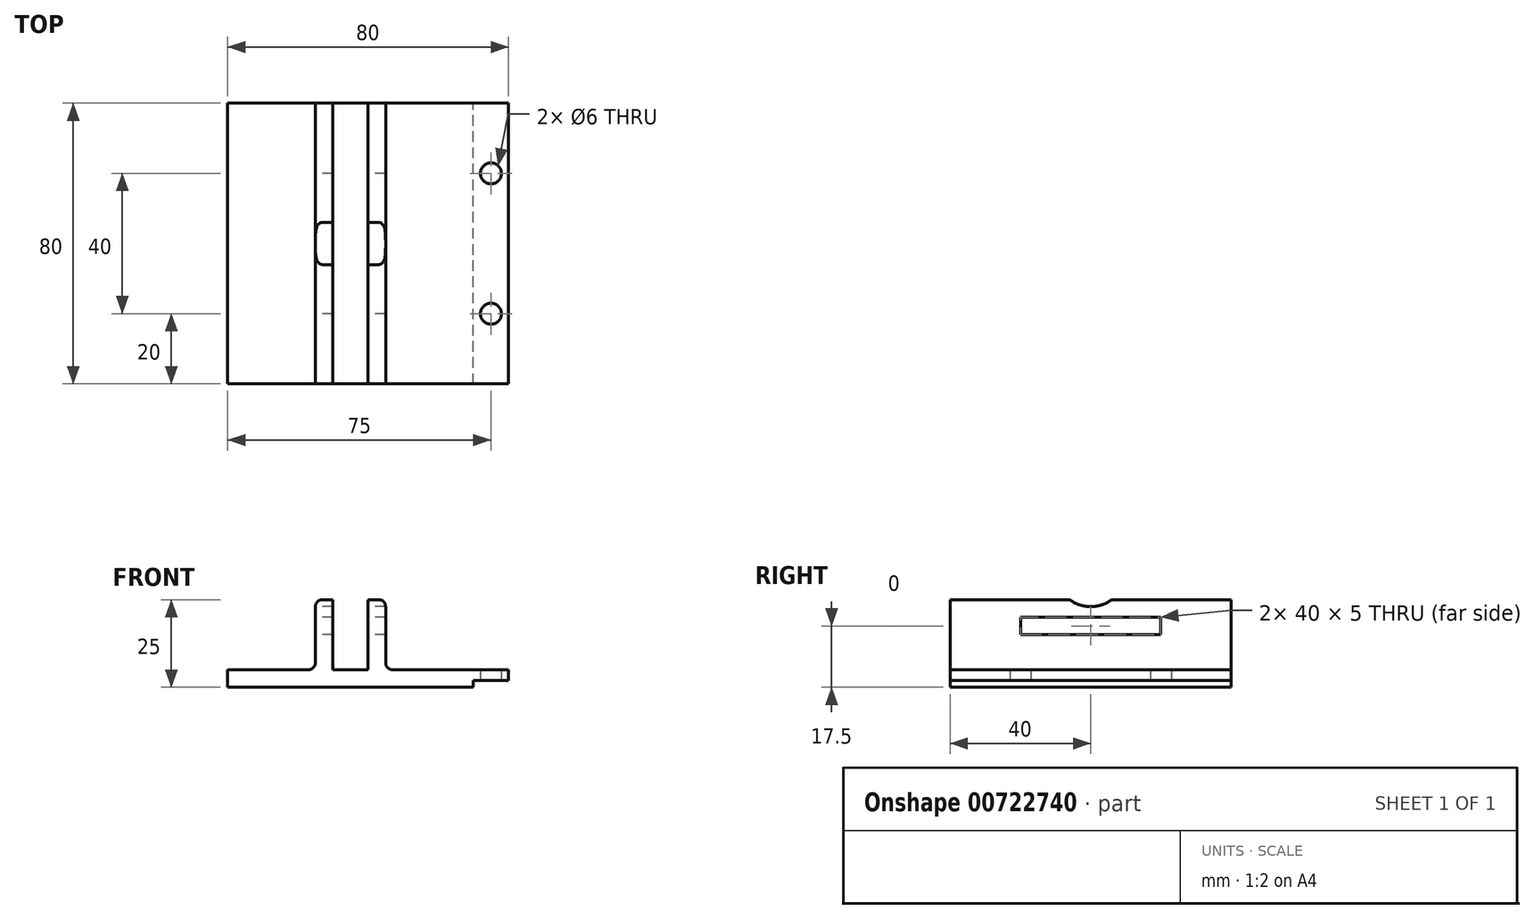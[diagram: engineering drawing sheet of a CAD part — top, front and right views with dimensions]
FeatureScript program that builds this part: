
annotation { "Feature Type Name" : "Feature", "Feature Type Description" : "" }
export const myFeature = defineFeature(function(context is Context, id is Id, definition is map)
    precondition{}
    {
        {
            var Q0;
            Q0=qCreatedBy(makeId("Front.planeOp"),FACE);
            var sketch = newSketch(context, id + "F0", { "sketchPlane" : qUnion([Q0])});
            skLineSegment(sketch, "E0.bottom", {"start": v(0, 0) * mm, "end": v(-10, 0) * mm, "construction": true});
            skLineSegment(sketch, "E0.top", {"start": v(0, 20) * mm, "end": v(-10, 20) * mm, "construction": true});
            skLineSegment(sketch, "E0.left", {"start": v(0, 0) * mm, "end": v(0, 20) * mm, "construction": true});
            skLineSegment(sketch, "E0.right", {"start": v(-10, 0) * mm, "end": v(-10, 20) * mm, "construction": true});
            skLineSegment(sketch, "E1.bottom", {"start": v(-10, 20) * mm, "end": v(-15, 20) * mm});
            skLineSegment(sketch, "E1.top", {"start": v(-10, 0) * mm, "end": v(-15, 0) * mm, "construction": true});
            skLineSegment(sketch, "E1.left", {"start": v(-10, 20) * mm, "end": v(-10, 0) * mm});
            skLineSegment(sketch, "E1.right", {"start": v(-15, 20) * mm, "end": v(-15, 0) * mm});
            skLineSegment(sketch, "E2.bottom", {"start": v(0, 20) * mm, "end": v(5, 20) * mm});
            skLineSegment(sketch, "E2.top", {"start": v(0, 0) * mm, "end": v(5, 0) * mm});
            skLineSegment(sketch, "E2.left", {"start": v(0, 20) * mm, "end": v(0, 0) * mm});
            skLineSegment(sketch, "E2.right", {"start": v(5, 20) * mm, "end": v(5, 0) * mm});
            skLineSegment(sketch, "E3.bottom", {"start": v(0, 0) * mm, "end": v(-40, 0) * mm});
            skLineSegment(sketch, "E3.top", {"start": v(0, -5) * mm, "end": v(-40, -5) * mm});
            skLineSegment(sketch, "E3.left", {"start": v(0, 0) * mm, "end": v(0, -5) * mm});
            skLineSegment(sketch, "E3.right", {"start": v(-40, 0) * mm, "end": v(-40, -5) * mm});
            skLineSegment(sketch, "E4.bottom", {"start": v(0, 0) * mm, "end": v(30, 0) * mm});
            skLineSegment(sketch, "E4.top", {"start": v(0, -5) * mm, "end": v(30, -5) * mm});
            skLineSegment(sketch, "E4.right", {"start": v(30, 0) * mm, "end": v(30, -5) * mm});
            skSolve(sketch);
        }
        {
            var Q0;
            Q0=qSketchRegion(id+"F0",true);
            extrude(context, id + "F1", {"entities" : qUnion([Q0]), "depth" : 80 * mm, "offsetDistance" : 25 * mm, "symmetric" : true});
        }
        {
            var Q0;
            Q0=makeQuery(id+"F1.opExtrude","SWEPT_EDGE",EDGE,{"disambiguationData":[OSD([sQuery(id+"F0.wireOp",EDGE,"E2.right"),sQuery(id+"F0.wireOp",EDGE,"E4.bottom")])]});
            var Q1;
            Q1=makeQuery(id+"F1.opExtrude","SWEPT_EDGE",EDGE,{"disambiguationData":[OSD([sQuery(id+"F0.wireOp",EDGE,"E1.right"),sQuery(id+"F0.wireOp",EDGE,"E3.bottom")])]});
            fillet(context, id + "F2", {"entities" : qUnion([Q0, Q1]), "radius" : 2 * mm, "tangentPropagation" : true, "allowEdgeOverflow" : false});
        }
        {
            var Q0;
            Q0=makeQuery(id+"F1.opExtrude","SWEPT_EDGE",EDGE,{"disambiguationData":[OSD([sQuery(id+"F0.wireOp",EDGE,"E1.bottom"),sQuery(id+"F0.wireOp",EDGE,"E1.right")])]});
            var Q1;
            Q1=makeQuery(id+"F1.opExtrude","SWEPT_EDGE",EDGE,{"disambiguationData":[OSD([sQuery(id+"F0.wireOp",EDGE,"E2.bottom"),sQuery(id+"F0.wireOp",EDGE,"E2.right")])]});
            fillet(context, id + "F3", {"entities" : qUnion([Q0, Q1]), "radius" : 2 * mm, "tangentPropagation" : true, "allowEdgeOverflow" : false});
        }
        {
            var Q0;
            Q0=makeQuery(id+"F1.opExtrude","SWEPT_FACE",FACE,{"disambiguationData":[OSD([sQuery(id+"F0.wireOp",EDGE,"E1.right")])]});
            var sketch = newSketch(context, id + "F4", { "sketchPlane" : qUnion([Q0])});
            skLineSegment(sketch, "E5", {"start": v(-40, 0) * mm, "end": v(-20, 0) * mm, "construction": true});
            skLineSegment(sketch, "E6", {"start": v(-20, 0) * mm, "end": v(-20, 10) * mm, "construction": true});
            skLineSegment(sketch, "E7.bottom", {"start": v(-20, 10) * mm, "end": v(20, 10) * mm});
            skLineSegment(sketch, "E7.top", {"start": v(-20, 15) * mm, "end": v(20, 15) * mm});
            skLineSegment(sketch, "E7.left", {"start": v(-20, 10) * mm, "end": v(-20, 15) * mm});
            skLineSegment(sketch, "E7.right", {"start": v(20, 10) * mm, "end": v(20, 15) * mm});
            skSolve(sketch);
        }
        {
            var Q0;
            Q0=qSketchRegion(id+"F4",true);
            extrude(context, id + "F5", {"entities" : qUnion([Q0]), "operationType" : NewBodyOperationType.REMOVE, "oppositeDirection" : true, "depth" : 25 * mm, "offsetDistance" : 25 * mm});
        }
        {
            var Q0;
            Q0=makeQuery(id+"F1.opExtrude","SWEPT_FACE",FACE,{"disambiguationData":[OSD([sQuery(id+"F0.wireOp",EDGE,"E4.bottom")])]});
            var sketch = newSketch(context, id + "F6", { "sketchPlane" : qUnion([Q0])});
            skLineSegment(sketch, "E8.bottom", {"start": v(30, 40) * mm, "end": v(40, 40) * mm});
            skLineSegment(sketch, "E8.top", {"start": v(30, -40) * mm, "end": v(40, -40) * mm});
            skLineSegment(sketch, "E8.left", {"start": v(30, 40) * mm, "end": v(30, -40) * mm});
            skLineSegment(sketch, "E8.right", {"start": v(40, 40) * mm, "end": v(40, -40) * mm});
            skSolve(sketch);
        }
        {
            var Q0;
            Q0 = qSketchRegion(id + "F6", true);
            extrude(context, id + "F7", {"entities" : qUnion([Q0]), "operationType" : NewBodyOperationType.ADD, "oppositeDirection" : true, "depth" : 3 * mm, "offsetDistance" : 25 * mm});
        }
        {
            var Q0;
            Q0=makeQuery(id+"F7.opExtrude","CAP_FACE",FACE,{"disambiguationData":[OSD([sQuery(id+"F6.wireOp",EDGE,"E8.bottom"),sQuery(id+"F6.wireOp",EDGE,"E8.top"),sQuery(id+"F6.wireOp",EDGE,"E8.left"),sQuery(id+"F6.wireOp",EDGE,"E8.right")])],"isStart":false});
            var sketch = newSketch(context, id + "F8", { "sketchPlane" : qUnion([Q0])});
            skLineSegment(sketch, "E9", {"start": v(30, 0) * mm, "end": v(35, 0) * mm, "construction": true});
            skLineSegment(sketch, "E10", {"start": v(35, 0) * mm, "end": v(35, 20) * mm, "construction": true});
            skCircle(sketch, "E11", {"center": v(35, 20) * mm, "radius": 3 * mm});
            skSolve(sketch);
        }
        {
            var Q0;
            Q0 = qSketchRegion(id + "F8", true);
            extrude(context, id + "F9", {"entities" : qUnion([Q0]), "oppositeDirection" : true, "depth" : 3 * mm, "offsetDistance" : 25 * mm});
        }
        {
            var Q0;
            Q0=makeQuery(id+"F9.opExtrude","SWEPT_BODY",BODY,{"disambiguationData":[OSD([sQuery(id+"F8.wireOp",EDGE,"E11")])]});
            var Q1;
            Q1=qCreatedBy(makeId("Front.planeOp"),FACE);
            mirror(context, id + "F10", {"entities" : qUnion([Q0]), "mirrorPlane" : qUnion([Q1])});
        }
        {
            var Q0;
            Q0=makeQuery(id+"F10.opPattern","COPY",BODY,{"derivedFrom":makeQuery(id+"F9.opExtrude","SWEPT_BODY",BODY,{"disambiguationData":[OSD([sQuery(id+"F8.wireOp",EDGE,"E11")])]}),"instanceName":"1"});
            var Q1;
            Q1=makeQuery(id+"F9.opExtrude","SWEPT_BODY",BODY,{"disambiguationData":[OSD([sQuery(id+"F8.wireOp",EDGE,"E11")])]});
            var Q2;
            Q2=makeQuery(id+"F1.opExtrude","SWEPT_BODY",BODY,{"disambiguationData":[OSD([sQuery(id+"F0.wireOp",EDGE,"E1.bottom"),sQuery(id+"F0.wireOp",EDGE,"E1.left"),sQuery(id+"F0.wireOp",EDGE,"E1.right"),sQuery(id+"F0.wireOp",EDGE,"E2.bottom"),sQuery(id+"F0.wireOp",EDGE,"E2.left"),sQuery(id+"F0.wireOp",EDGE,"E2.right"),sQuery(id+"F0.wireOp",EDGE,"E3.bottom"),sQuery(id+"F0.wireOp",EDGE,"E3.top"),sQuery(id+"F0.wireOp",EDGE,"E3.right"),sQuery(id+"F0.wireOp",EDGE,"E4.bottom"),sQuery(id+"F0.wireOp",EDGE,"E4.top"),sQuery(id+"F0.wireOp",EDGE,"E4.right")])]});
            booleanBodies(context, id + "F11", {"operationType" : BooleanOperationType.SUBTRACTION, "tools" : qUnion([Q0, Q1]), "targets" : qUnion([Q2])});
        }
        {
            var Q0;
            Q0=makeQuery(id+"F1.opExtrude","SWEPT_FACE",FACE,{"disambiguationData":[OSD([sQuery(id+"F0.wireOp",EDGE,"E1.right")])]});
            var sketch = newSketch(context, id + "F12", { "sketchPlane" : qUnion([Q0])});
            skLineSegment(sketch, "E12", {"start": v(0, 0) * mm, "end": v(0, 28) * mm, "construction": true});
            skCircle(sketch, "E13", {"center": v(0, 28) * mm, "radius": 10 * mm});
            skSolve(sketch);
        }
        {
            var Q0;
            Q0 = qSketchRegion(id + "F12", true);
            extrude(context, id + "F13", {"entities" : qUnion([Q0]), "operationType" : NewBodyOperationType.REMOVE, "oppositeDirection" : true, "depth" : 25 * mm, "offsetDistance" : 25 * mm});
        }
    });
